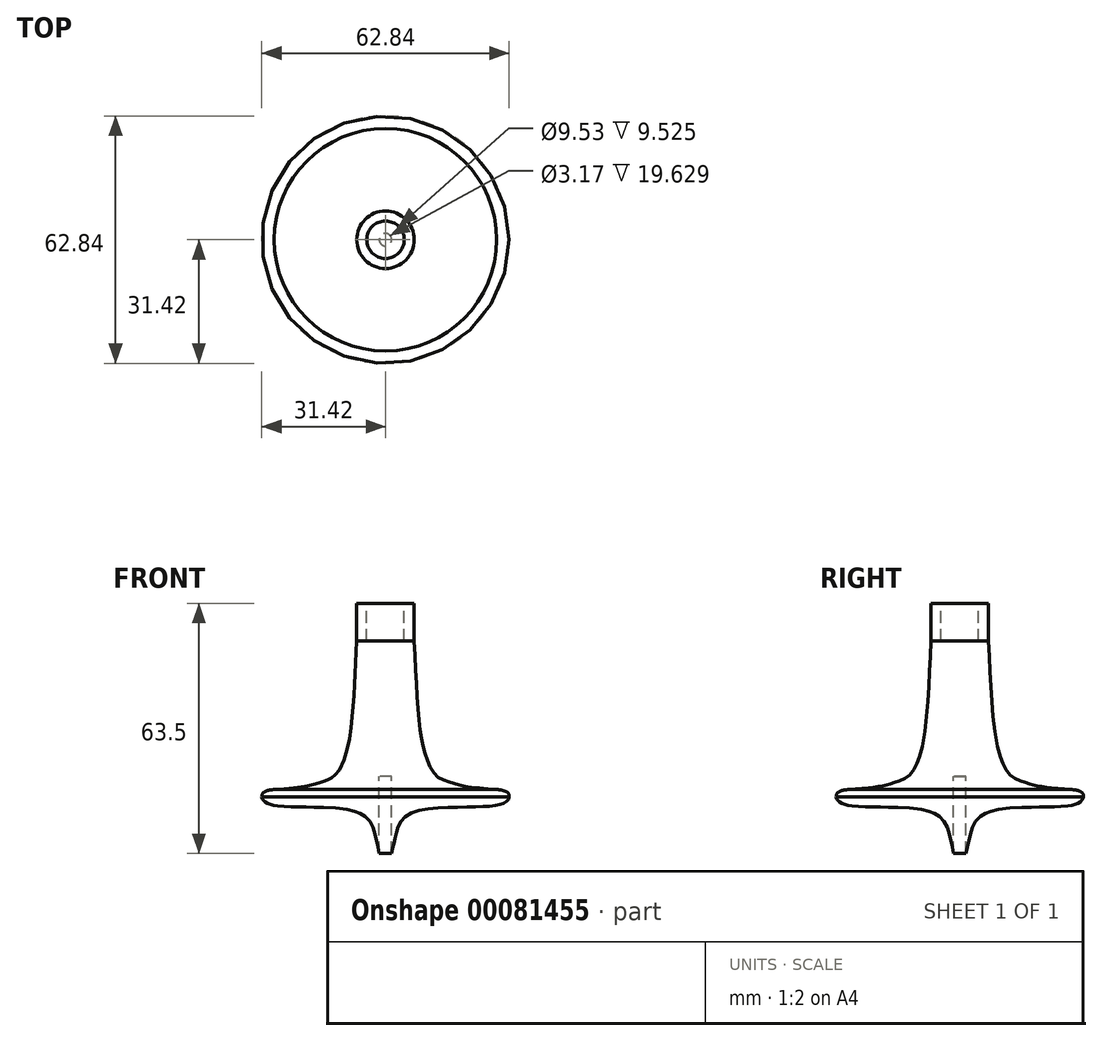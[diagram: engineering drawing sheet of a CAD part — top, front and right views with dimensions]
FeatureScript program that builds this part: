
annotation { "Feature Type Name" : "Feature", "Feature Type Description" : "" }
export const myFeature = defineFeature(function(context is Context, id is Id, definition is map)
    precondition{}
    {
        {
            var Q0;
            Q0=qCreatedBy(makeId("Front.planeOp"),FACE);
            var sketch = newSketch(context, id + "F0", { "sketchPlane" : qUnion([Q0])});
            skFitSpline(sketch, "E0", {"points": [v(1.59, -12.96) * mm, v(2.53, -8.6) * mm, v(5.32, -3.4) * mm, v(18.39, -1.2) * mm, v(27.76, -0.81) * mm, v(30.36, 0) * mm, v(31.36, 1.08) * mm, v(31.26, 2.18) * mm, v(30.56, 2.78) * mm, v(29.16, 3.18) * mm, v(28.26, 3.28) * mm, v(28.16, 3.28) * mm], "startDerivative": vector(7.51, 36.72) * mm, "endDerivative": vector(-4.46, -0.16) * mm});
            skLineSegment(sketch, "E1", {"start": v(4.76, 50.54) * mm, "end": v(4.76, 41.01) * mm});
            skLineSegment(sketch, "E2", {"start": v(4.76, 41.01) * mm, "end": v(0, 41.01) * mm});
            skLineSegment(sketch, "E3", {"start": v(4.76, 50.54) * mm, "end": v(7.3, 50.54) * mm});
            skLineSegment(sketch, "E4", {"start": v(7.3, 50.54) * mm, "end": v(7.3, 41) * mm});
            skLineSegment(sketch, "E5", {"start": v(1.59, -12.96) * mm, "end": v(1.59, 6.67) * mm});
            skLineSegment(sketch, "E6", {"start": v(1.59, 6.67) * mm, "end": v(0, 6.67) * mm});
            skLineSegment(sketch, "E7", {"start": v(0, 41.01) * mm, "end": v(0, 6.67) * mm});
            skFitSpline(sketch, "E8", {"points": [v(28.26, 3.28) * mm, v(20.37, 4.09) * mm, v(16.66, 5.03) * mm, v(12.95, 6.77) * mm, v(10.2, 11.9) * mm, v(8.61, 20.19) * mm, v(7.3, 41) * mm], "startDerivative": vector(-51.54, 3.87) * mm, "endDerivative": vector(-4.02, 84.6) * mm});
            skLineSegment(sketch, "E9", {"start": v(31.42, 1.46) * mm, "end": v(17.78, 1.46) * mm});
            skPoint(sketch, "E10.startSnap0", {"position": v(1.59, -3.15) * mm});
            skSolve(sketch);
        }
        {
            var Q0;
            Q0=qSketchRegion(id+"F0",true);
            var Q1;
            Q1=sQuery(id+"F0.wireOp",EDGE,"E7");
            revolve(context, id + "F1", {"entities" : qUnion([Q0]), "axis" : qUnion([Q1]), "revolveType" : RevolveType.FULL});
        }
    });
